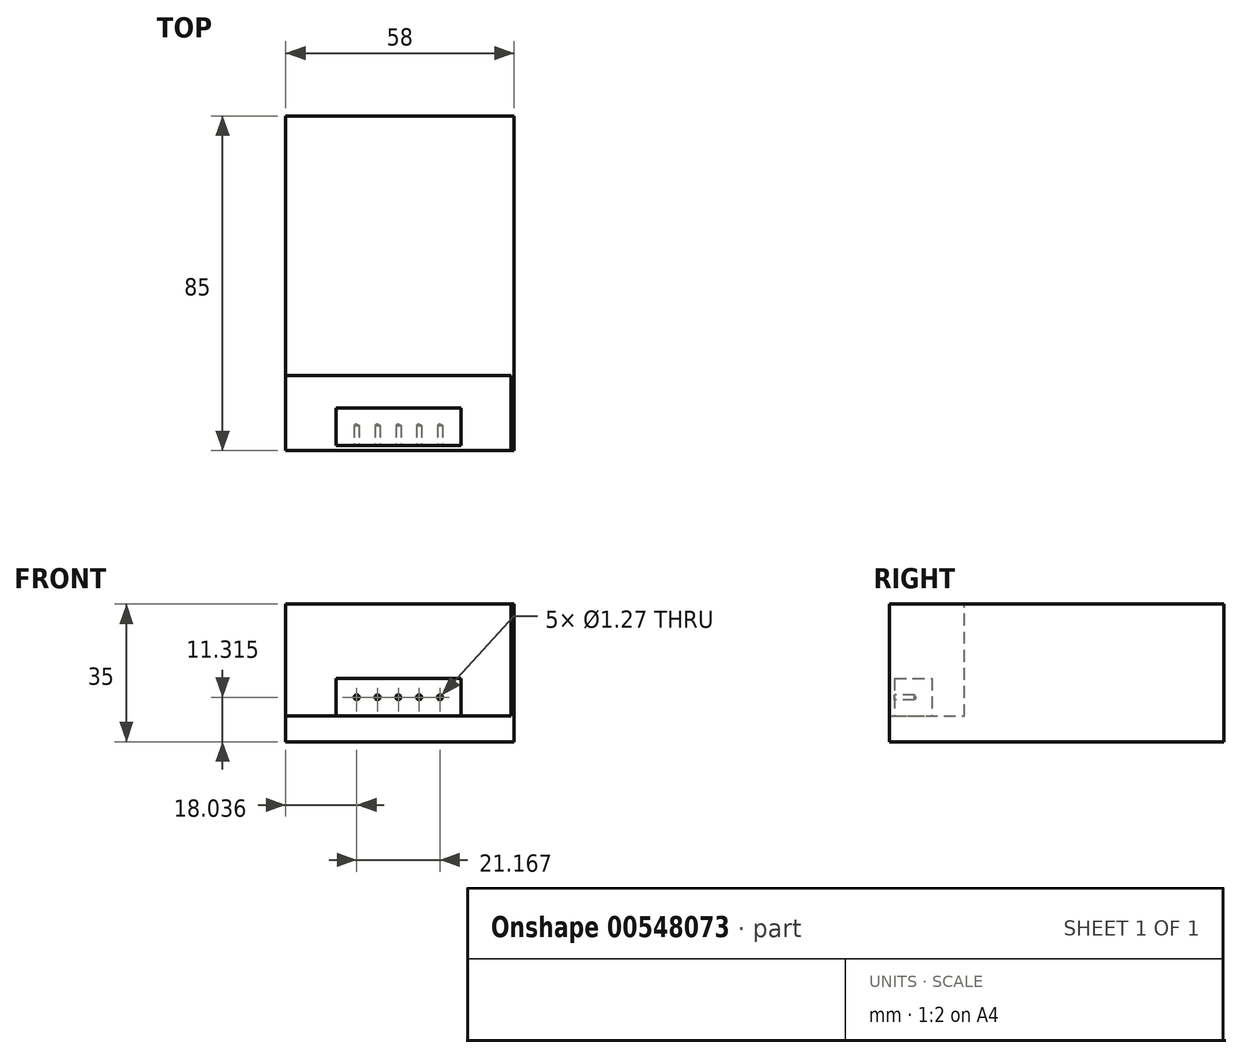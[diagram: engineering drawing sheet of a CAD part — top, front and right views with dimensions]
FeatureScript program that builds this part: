
annotation { "Feature Type Name" : "Feature", "Feature Type Description" : "" }
export const myFeature = defineFeature(function(context is Context, id is Id, definition is map)
    precondition{}
    {
        {
            var Q0;
            Q0=qCreatedBy(makeId("Top.planeOp"),FACE);
            var sketch = newSketch(context, id + "F0", { "sketchPlane" : qUnion([Q0])});
            skLineSegment(sketch, "E0.bottom", {"start": v(29, -42.5) * mm, "end": v(-29, -42.5) * mm});
            skLineSegment(sketch, "E0.top", {"start": v(29, 42.5) * mm, "end": v(-29, 42.5) * mm});
            skLineSegment(sketch, "E0.left", {"start": v(29, -42.5) * mm, "end": v(29, 42.5) * mm});
            skLineSegment(sketch, "E0.right", {"start": v(-29, -42.5) * mm, "end": v(-29, 42.5) * mm});
            skPoint(sketch, "E0.middle", {"position": v(0, 0) * mm});
            skSolve(sketch);
        }
        {
            var Q0;
            Q0 = qSketchRegion(id + "F0", true);
            extrude(context, id + "F1", {"entities" : qUnion([Q0]), "depth" : 35 * mm, "offsetDistance" : 25.4 * mm});
        }
        {
            var Q0;
            Q0=makeQuery(id+"F1.opExtrude","CAP_FACE",FACE,{"disambiguationData":[OSD([sQuery(id+"F0.wireOp",EDGE,"E0.bottom"),sQuery(id+"F0.wireOp",EDGE,"E0.top"),sQuery(id+"F0.wireOp",EDGE,"E0.left"),sQuery(id+"F0.wireOp",EDGE,"E0.right")])],"isStart":false});
            var sketch = newSketch(context, id + "F2", { "sketchPlane" : qUnion([Q0])});
            skLineSegment(sketch, "E1.bottom", {"start": v(-29, -42.5) * mm, "end": v(28.24, -42.5) * mm});
            skLineSegment(sketch, "E1.top", {"start": v(-29, -23.45) * mm, "end": v(28.24, -23.45) * mm});
            skLineSegment(sketch, "E1.left", {"start": v(-29, -42.5) * mm, "end": v(-29, -23.45) * mm});
            skLineSegment(sketch, "E1.right", {"start": v(28.24, -42.5) * mm, "end": v(28.24, -23.45) * mm});
            skSolve(sketch);
        }
        {
            var Q0;
            Q0 = qSketchRegion(id + "F2", true);
            extrude(context, id + "F3", {"entities" : qUnion([Q0]), "operationType" : NewBodyOperationType.REMOVE, "oppositeDirection" : true, "depth" : 28.45 * mm, "offsetDistance" : 25.4 * mm});
        }
        {
            var Q0;
            Q0=makeQuery(id+"F3.boolean.opBoolean","COPY",FACE,{"derivedFrom":makeQuery(id+"F3.opExtrude","CAP_FACE",FACE,{"disambiguationData":[OSD([sQuery(id+"F2.wireOp",EDGE,"E1.bottom"),sQuery(id+"F2.wireOp",EDGE,"E1.top"),sQuery(id+"F2.wireOp",EDGE,"E1.left"),sQuery(id+"F2.wireOp",EDGE,"E1.right")])],"isStart":false})});
            var sketch = newSketch(context, id + "F4", { "sketchPlane" : qUnion([Q0])});
            skLineSegment(sketch, "E2.bottom", {"start": v(-16.26, -41.23) * mm, "end": v(15.5, -41.23) * mm});
            skLineSegment(sketch, "E2.top", {"start": v(-16.26, -31.7) * mm, "end": v(15.5, -31.7) * mm});
            skLineSegment(sketch, "E2.left", {"start": v(-16.26, -41.23) * mm, "end": v(-16.26, -31.7) * mm});
            skLineSegment(sketch, "E2.right", {"start": v(15.5, -41.23) * mm, "end": v(15.5, -31.7) * mm});
            skLineSegment(sketch, "E3", {"start": v(-16.26, -41.23) * mm, "end": v(-29, -41.23) * mm, "construction": true});
            skLineSegment(sketch, "E4", {"start": v(15.5, -41.23) * mm, "end": v(28.24, -41.23) * mm, "construction": true});
            skSolve(sketch);
        }
        {
            var Q0;
            Q0 = qSketchRegion(id + "F4", true);
            extrude(context, id + "F5", {"entities" : qUnion([Q0]), "operationType" : NewBodyOperationType.ADD, "depth" : 9.52 * mm, "offsetDistance" : 25.4 * mm});
        }
        {
            var Q0;
            Q0=makeQuery(id+"F5.opExtrude","SWEPT_FACE",FACE,{"disambiguationData":[OSD([sQuery(id+"F4.wireOp",EDGE,"E2.bottom")])]});
            var sketch = newSketch(context, id + "F6", { "sketchPlane" : qUnion([Q0])});
            skLineSegment(sketch, "E5", {"start": v(-16.26, 11.31) * mm, "end": v(-10.96, 11.31) * mm, "construction": true});
            skLineSegment(sketch, "E6", {"start": v(-10.96, 11.31) * mm, "end": v(-5.67, 11.31) * mm, "construction": true});
            skLineSegment(sketch, "E7", {"start": v(-5.67, 11.31) * mm, "end": v(-0.38, 11.31) * mm, "construction": true});
            skLineSegment(sketch, "E8", {"start": v(-0.38, 11.31) * mm, "end": v(4.91, 11.31) * mm, "construction": true});
            skLineSegment(sketch, "E9", {"start": v(4.91, 11.31) * mm, "end": v(10.2, 11.31) * mm, "construction": true});
            skLineSegment(sketch, "E10", {"start": v(10.2, 11.31) * mm, "end": v(15.5, 11.31) * mm, "construction": true});
            skPoint(sketch, "E11", {"position": v(-10.96, 11.31) * mm});
            skPoint(sketch, "E12", {"position": v(-5.67, 11.31) * mm});
            skPoint(sketch, "E13", {"position": v(-0.38, 11.31) * mm});
            skPoint(sketch, "E14", {"position": v(4.91, 11.31) * mm});
            skPoint(sketch, "E15", {"position": v(10.2, 11.31) * mm});
            skSolve(sketch);
        }
        {
            var Q0;
            Q0=sQuery(id+"F6.wireOp",VERTEX,"E11");
            var Q1;
            Q1=sQuery(id+"F6.wireOp",VERTEX,"E12");
            var Q2;
            Q2=sQuery(id+"F6.wireOp",VERTEX,"E13");
            var Q3;
            Q3=sQuery(id+"F6.wireOp",VERTEX,"E14");
            var Q4;
            Q4=sQuery(id+"F6.wireOp",VERTEX,"E15");
            var Q5;
            Q5=makeQuery(id+"F1.opExtrude","SWEPT_BODY",BODY,{"disambiguationData":[OSD([sQuery(id+"F0.wireOp",EDGE,"E0.bottom"),sQuery(id+"F0.wireOp",EDGE,"E0.top"),sQuery(id+"F0.wireOp",EDGE,"E0.left"),sQuery(id+"F0.wireOp",EDGE,"E0.right")])]});
            hole(context, id + "F7", {"style" : HoleStyle.SIMPLE, "endStyle" : HoleEndStyle.BLIND, "holeDiameter" : 1.27 * mm, "majorDiameter" : 6.35 * mm, "holeDepth" : 5.08 * mm, "isTappedThrough" : true, "tappedDepth" : 12.7 * mm, "tapClearance" : 3, "locations" : qUnion([Q0, Q1, Q2, Q3, Q4]), "scope" : qUnion([Q5])});
        }
    });
